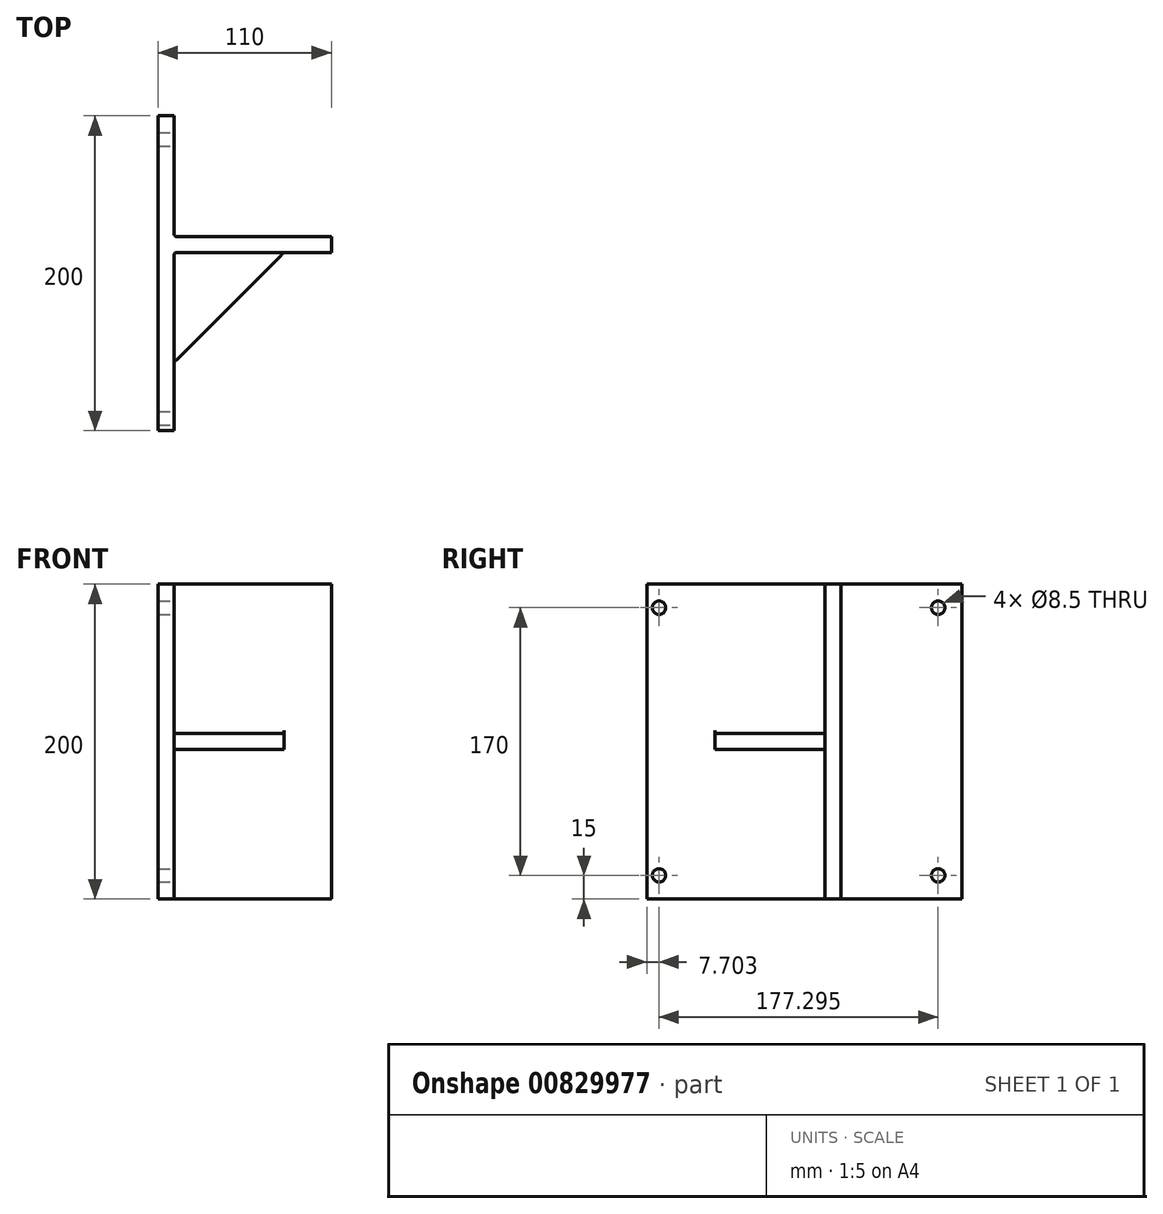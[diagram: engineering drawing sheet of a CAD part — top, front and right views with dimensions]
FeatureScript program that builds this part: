
annotation { "Feature Type Name" : "Feature", "Feature Type Description" : "" }
export const myFeature = defineFeature(function(context is Context, id is Id, definition is map)
    precondition{}
    {
        {
            var Q0;
            Q0=qCreatedBy(makeId("Top.planeOp"),FACE);
            var sketch = newSketch(context, id + "F0", { "sketchPlane" : qUnion([Q0])});
            skLineSegment(sketch, "E0", {"start": v(0, 103.65) * mm, "end": v(0, -96.35) * mm});
            skLineSegment(sketch, "E1", {"start": v(10, -96.35) * mm, "end": v(0, -96.35) * mm});
            skLineSegment(sketch, "E2", {"start": v(10, -96.35) * mm, "end": v(10, 16.85) * mm});
            skLineSegment(sketch, "E3", {"start": v(0, 103.65) * mm, "end": v(10, 103.65) * mm});
            skLineSegment(sketch, "E4", {"start": v(10, 26.85) * mm, "end": v(10, 103.65) * mm});
            skLineSegment(sketch, "E5", {"start": v(10, 16.85) * mm, "end": v(110, 16.85) * mm});
            skLineSegment(sketch, "E6", {"start": v(10, 26.85) * mm, "end": v(110, 26.85) * mm});
            skLineSegment(sketch, "E7", {"start": v(110, 16.85) * mm, "end": v(110, 26.85) * mm});
            skSolve(sketch);
        }
        {
            var Q0;
            Q0=makeQuery(id+"F0.imprint","IMPRINT",FACE,{"disambiguationData":[TD([[makeQuery(id+"F0.imprint","IMPRINT",EDGE,{"derivedFrom":sQuery(id+"F0.wireOp",EDGE,"E0")}),1.0]])]});
            extrude(context, id + "F1", {"entities" : qUnion([Q0]), "endBound" : BoundingType.SYMMETRIC, "depth" : 200 * mm, "offsetDistance" : 25 * mm});
        }
        {
            var Q0;
            Q0=makeQuery(id+"F1.opExtrude","SWEPT_FACE",FACE,{"disambiguationData":[OSD([sQuery(id+"F0.wireOp",EDGE,"E2")])]});
            var sketch = newSketch(context, id + "F2", { "sketchPlane" : qUnion([Q0])});
            skLineSegment(sketch, "E8", {"start": v(16.85, -5) * mm, "end": v(-53.15, -5) * mm});
            skLineSegment(sketch, "E9", {"start": v(-53.15, -5) * mm, "end": v(-53.15, 5) * mm});
            skLineSegment(sketch, "E10", {"start": v(-53.15, 5) * mm, "end": v(16.85, 5) * mm});
            skSolve(sketch);
        }
        {
            var Q0;
            {var subQ0=sQuery(id+"F2.wireOp",EDGE,"E8");Q0=makeQuery(id+"F2.imprint","IMPRINT",FACE,{"disambiguationData":[TD([[makeQuery(id+"F2.imprint","IMPRINT",EDGE,{"derivedFrom":subQ0}),-1.0]])]});}
            extrude(context, id + "F3", {"entities" : qUnion([Q0]), "operationType" : NewBodyOperationType.ADD, "depth" : 100 * mm, "offsetDistance" : 25 * mm});
        }
        {
            var Q0;
            Q0=makeQuery(id+"F3.opExtrude","SWEPT_FACE",FACE,{"disambiguationData":[OSD([sQuery(id+"F2.wireOp",EDGE,"E10")])]});
            var sketch = newSketch(context, id + "F4", { "sketchPlane" : qUnion([Q0])});
            skLineSegment(sketch, "E11", {"start": v(110, 16.85) * mm, "end": v(110, -53.15) * mm});
            skLineSegment(sketch, "E12", {"start": v(110, -53.15) * mm, "end": v(10, -53.15) * mm});
            skLineSegment(sketch, "E13", {"start": v(10, -53.15) * mm, "end": v(80, 16.85) * mm});
            skSolve(sketch);
        }
        {
            var Q0;
            {var subQ0=sQuery(id+"F0.wireOp",EDGE,"E5");var subQ1=sQuery(id+"F0.wireOp",EDGE,"E2");Q0=makeQuery(id+"F3.boolean.opBoolean","SPLIT",EDGE,{"disambiguationData":[TD([makeQuery(id+"F3.opExtrude","SWEPT_FACE",FACE,{"disambiguationData":[OSD([sQuery(id+"F2.wireOp",EDGE,"E10")])]})])],"derivedFrom":makeQuery(id+"F1.opExtrude","SWEPT_EDGE",EDGE,{"disambiguationData":[OSD([subQ1,subQ0])]})});}
            var Q1;
            {var subQ0=sQuery(id+"F0.wireOp",EDGE,"E5");var subQ1=sQuery(id+"F0.wireOp",EDGE,"E2");Q1=makeQuery(id+"F3.boolean.opBoolean","SPLIT",EDGE,{"disambiguationData":[TD([makeQuery(id+"F3.opExtrude","SWEPT_FACE",FACE,{"disambiguationData":[OSD([sQuery(id+"F2.wireOp",EDGE,"E8")])]})])],"derivedFrom":makeQuery(id+"F1.opExtrude","SWEPT_EDGE",EDGE,{"disambiguationData":[OSD([subQ1,subQ0])]})});}
            fillet(context, id + "F5", {"entities" : qUnion([Q0, Q1]), "radius" : 2 * mm, "tangentPropagation" : true, "allowEdgeOverflow" : false});
        }
        {
            var Q0;
            {var subQ0=sQuery(id+"F4.wireOp",EDGE,"E11");Q0=makeQuery(id+"F4.imprint","IMPRINT",FACE,{"disambiguationData":[TD([[makeQuery(id+"F4.imprint","IMPRINT",EDGE,{"derivedFrom":subQ0}),1.0]])]});}
            extrude(context, id + "F6", {"entities" : qUnion([Q0]), "operationType" : NewBodyOperationType.REMOVE, "oppositeDirection" : true, "depth" : 25 * mm, "offsetDistance" : 25 * mm});
        }
        {
            var Q0;
            Q0=makeQuery(id+"F3.opExtrude","CAP_EDGE",EDGE,{"disambiguationData":[OSD([sQuery(id+"F2.wireOp",EDGE,"E10")])],"isStart":true});
            var Q1;
            Q1=makeQuery(id+"F3.opExtrude","SWEPT_EDGE",EDGE,{"disambiguationData":[OSD([sQuery(id+"F0.wireOp",EDGE,"E2"),sQuery(id+"F0.wireOp",EDGE,"E5"),sQuery(id+"F2.wireOp",EDGE,"E10")])]});
            var Q2;
            Q2=makeQuery(id+"F3.opExtrude","CAP_EDGE",EDGE,{"disambiguationData":[OSD([sQuery(id+"F2.wireOp",EDGE,"E8")])],"isStart":true});
            var Q3;
            Q3=makeQuery(id+"F3.opExtrude","SWEPT_EDGE",EDGE,{"disambiguationData":[OSD([sQuery(id+"F0.wireOp",EDGE,"E2"),sQuery(id+"F0.wireOp",EDGE,"E5"),sQuery(id+"F2.wireOp",EDGE,"E8")])]});
            var Q4;
            Q4=makeQuery(id+"F1.opExtrude","SWEPT_EDGE",EDGE,{"disambiguationData":[OSD([sQuery(id+"F0.wireOp",EDGE,"E4"),sQuery(id+"F0.wireOp",EDGE,"E6")])]});
            fillet(context, id + "F7", {"entities" : qUnion([Q0, Q1, Q2, Q3, Q4]), "radius" : 2 * mm, "tangentPropagation" : true, "allowEdgeOverflow" : false});
        }
        {
            var Q0;
            Q0=makeQuery(id+"F1.opExtrude","SWEPT_FACE",FACE,{"disambiguationData":[OSD([sQuery(id+"F0.wireOp",EDGE,"E4")])]});
            var sketch = newSketch(context, id + "F8", { "sketchPlane" : qUnion([Q0])});
            skPoint(sketch, "E14", {"position": v(88.65, 85) * mm});
            skPoint(sketch, "E15.MirrorP", {"position": v(88.65, -85) * mm});
            skPoint(sketch, "E16.MirrorP", {"position": v(-88.65, 85) * mm});
            skPoint(sketch, "E17.MirrorP", {"position": v(-88.65, -85) * mm});
            skSolve(sketch);
        }
        {
            var Q0;
            Q0=sQuery(id+"F8.wireOp",VERTEX,"E14");
            var Q1;
            Q1=sQuery(id+"F8.wireOp",VERTEX,"E15.MirrorP");
            var Q2;
            Q2=sQuery(id+"F8.wireOp",VERTEX,"E17.MirrorP");
            var Q3;
            Q3=sQuery(id+"F8.wireOp",VERTEX,"E16.MirrorP");
            var Q4;
            Q4=makeQuery(id+"F1.opExtrude","SWEPT_BODY",BODY,{"disambiguationData":[OSD([sQuery(id+"F0.wireOp",EDGE,"E0"),sQuery(id+"F0.wireOp",EDGE,"E1"),sQuery(id+"F0.wireOp",EDGE,"E2"),sQuery(id+"F0.wireOp",EDGE,"E3"),sQuery(id+"F0.wireOp",EDGE,"E4"),sQuery(id+"F0.wireOp",EDGE,"E5"),sQuery(id+"F0.wireOp",EDGE,"E6"),sQuery(id+"F0.wireOp",EDGE,"E7")])]});
            hole(context, id + "F9", {"style" : HoleStyle.SIMPLE, "endStyle" : HoleEndStyle.THROUGH, "holeDiameter" : 8.5 * mm, "majorDiameter" : 5 * mm, "isTappedThrough" : true, "tappedDepth" : 12 * mm, "tapClearance" : 3, "locations" : qUnion([Q0, Q1, Q2, Q3]), "scope" : qUnion([Q4])});
        }
    });
